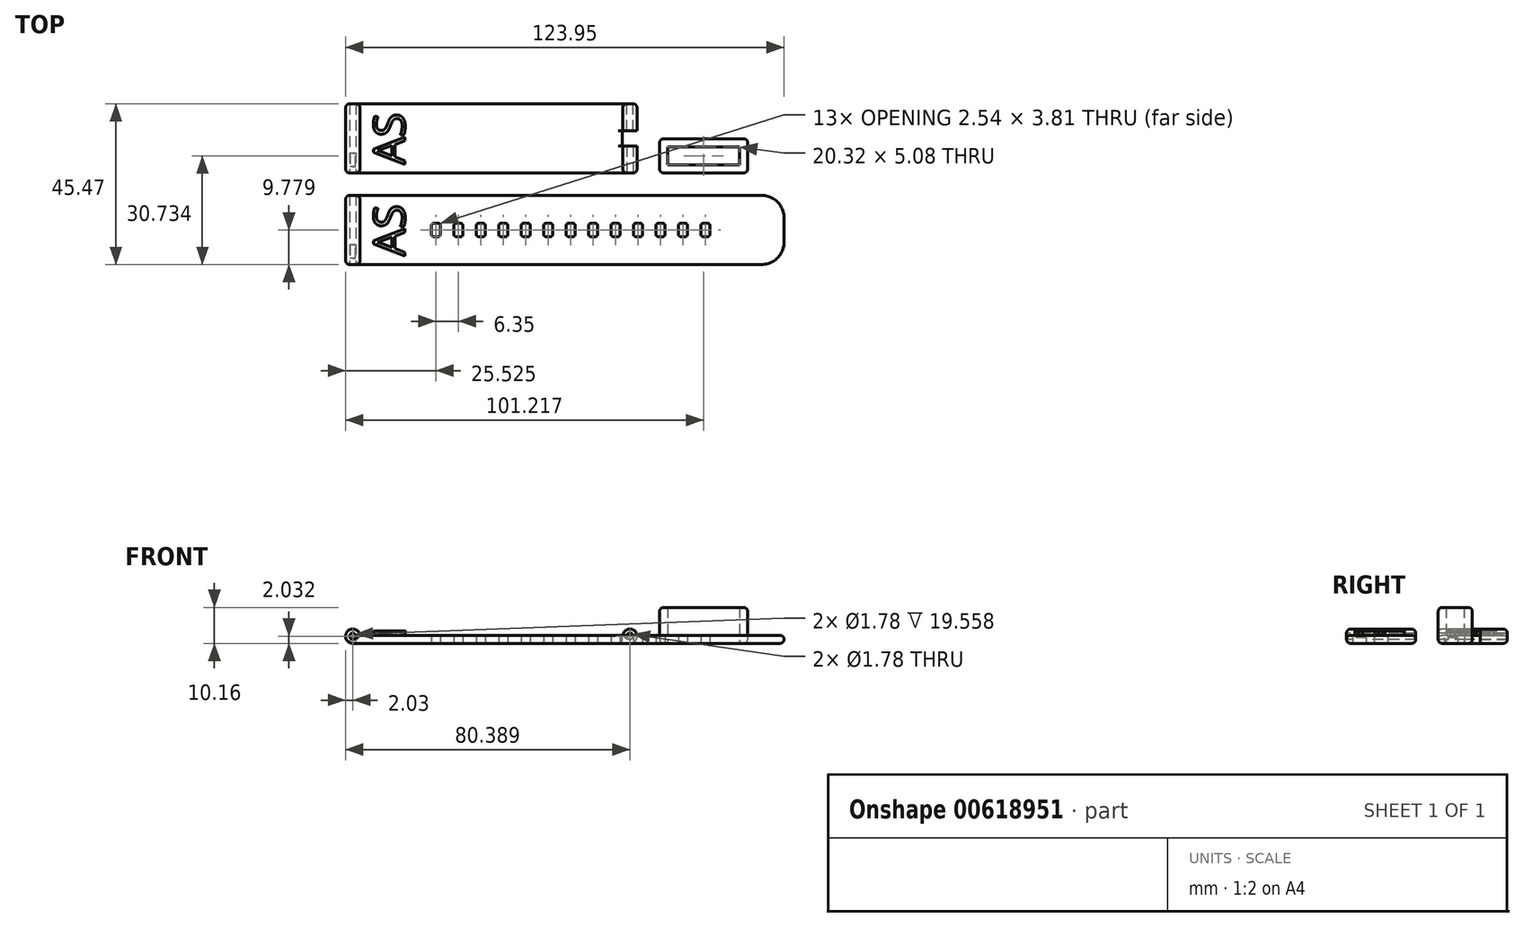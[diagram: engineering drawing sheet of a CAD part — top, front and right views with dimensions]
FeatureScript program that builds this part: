
annotation { "Feature Type Name" : "Feature", "Feature Type Description" : "" }
export const myFeature = defineFeature(function(context is Context, id is Id, definition is map)
    precondition{}
    {
        {
            var Q0;
            Q0=qCreatedBy(makeId("Top.planeOp"),FACE);
            var sketch = newSketch(context, id + "F0", { "sketchPlane" : qUnion([Q0])});
            skLineSegment(sketch, "E0.bottom", {"start": v(0, 0) * mm, "end": v(115.57, 0) * mm});
            skLineSegment(sketch, "E0.top", {"start": v(0, 19.56) * mm, "end": v(115.57, 19.56) * mm});
            skLineSegment(sketch, "E0.left", {"start": v(0, 0) * mm, "end": v(0, 19.56) * mm});
            skLineSegment(sketch, "E0.right", {"start": v(121.92, 6.35) * mm, "end": v(121.92, 13.2) * mm});
            skPoint(sketch, "E1.visualSharp", {"position": v(121.92, 19.56) * mm});
            skArc(sketch, "E1.filletArc", {"start": v(121.92, 13.2) * mm, "mid": v(120.06, 17.7) * mm, "end": v(115.57, 19.56) * mm});
            skPoint(sketch, "E2.visualSharp", {"position": v(121.92, 0) * mm});
            skArc(sketch, "E2.filletArc", {"start": v(115.57, 0) * mm, "mid": v(120.06, 1.86) * mm, "end": v(121.92, 6.35) * mm});
            skLineSegment(sketch, "E3.bottom", {"start": v(24.13, 7.87) * mm, "end": v(22.86, 7.87) * mm});
            skLineSegment(sketch, "E3.top", {"start": v(24.13, 11.68) * mm, "end": v(22.86, 11.68) * mm});
            skLineSegment(sketch, "E3.left", {"start": v(24.77, 8.5) * mm, "end": v(24.77, 11.05) * mm});
            skLineSegment(sketch, "E3.right", {"start": v(22.23, 8.5) * mm, "end": v(22.23, 11.05) * mm});
            skPoint(sketch, "E3.middle", {"position": v(23.5, 9.78) * mm});
            skPoint(sketch, "E3.middle.positionSnap0", {"position": v(0, 9.78) * mm});
            skPoint(sketch, "E3.centerSnap0", {"position": v(0, 9.78) * mm});
            skPoint(sketch, "E4.visualSharp", {"position": v(22.23, 11.68) * mm});
            skArc(sketch, "E4.filletArc", {"start": v(22.86, 11.68) * mm, "mid": v(22.41, 11.5) * mm, "end": v(22.22, 11.05) * mm});
            skPoint(sketch, "E5.visualSharp", {"position": v(24.77, 11.68) * mm});
            skArc(sketch, "E5.filletArc", {"start": v(24.77, 11.05) * mm, "mid": v(24.58, 11.5) * mm, "end": v(24.13, 11.68) * mm});
            skPoint(sketch, "E6.visualSharp", {"position": v(24.77, 7.87) * mm});
            skArc(sketch, "E6.filletArc", {"start": v(24.13, 7.87) * mm, "mid": v(24.58, 8.06) * mm, "end": v(24.77, 8.5) * mm});
            skPoint(sketch, "E7.visualSharp", {"position": v(22.23, 7.87) * mm});
            skArc(sketch, "E7.filletArc", {"start": v(22.23, 8.5) * mm, "mid": v(22.41, 8.06) * mm, "end": v(22.86, 7.87) * mm});
            skPoint(sketch, "E8.1.0.0", {"position": v(28.58, 7.87) * mm});
            skPoint(sketch, "E8.1.0.1", {"position": v(31.12, 7.87) * mm});
            skPoint(sketch, "E8.1.0.2", {"position": v(28.58, 11.68) * mm});
            skPoint(sketch, "E8.1.0.3", {"position": v(31.12, 11.68) * mm});
            skPoint(sketch, "E8.1.0.4", {"position": v(29.85, 9.78) * mm});
            skLineSegment(sketch, "E8.1.0.5", {"start": v(30.48, 11.68) * mm, "end": v(29.21, 11.68) * mm});
            skLineSegment(sketch, "E8.1.0.6", {"start": v(31.12, 8.5) * mm, "end": v(31.12, 11.05) * mm});
            skLineSegment(sketch, "E8.1.0.7", {"start": v(28.58, 8.5) * mm, "end": v(28.58, 11.05) * mm});
            skArc(sketch, "E8.1.0.8", {"start": v(31.12, 11.05) * mm, "mid": v(30.93, 11.5) * mm, "end": v(30.48, 11.68) * mm});
            skArc(sketch, "E8.1.0.9", {"start": v(29.21, 11.68) * mm, "mid": v(28.76, 11.5) * mm, "end": v(28.57, 11.05) * mm});
            skArc(sketch, "E8.1.0.10", {"start": v(30.48, 7.87) * mm, "mid": v(30.93, 8.06) * mm, "end": v(31.12, 8.5) * mm});
            skLineSegment(sketch, "E8.1.0.11", {"start": v(30.48, 7.87) * mm, "end": v(29.21, 7.87) * mm});
            skArc(sketch, "E8.1.0.12", {"start": v(28.58, 8.5) * mm, "mid": v(28.76, 8.06) * mm, "end": v(29.21, 7.87) * mm});
            skPoint(sketch, "E8.2.0.0", {"position": v(34.93, 7.87) * mm});
            skPoint(sketch, "E8.2.0.1", {"position": v(37.47, 7.87) * mm});
            skPoint(sketch, "E8.2.0.2", {"position": v(34.93, 11.68) * mm});
            skPoint(sketch, "E8.2.0.3", {"position": v(37.47, 11.68) * mm});
            skPoint(sketch, "E8.2.0.4", {"position": v(36.2, 9.78) * mm});
            skLineSegment(sketch, "E8.2.0.5", {"start": v(36.83, 11.68) * mm, "end": v(35.56, 11.68) * mm});
            skLineSegment(sketch, "E8.2.0.6", {"start": v(37.47, 8.5) * mm, "end": v(37.47, 11.05) * mm});
            skLineSegment(sketch, "E8.2.0.7", {"start": v(34.93, 8.5) * mm, "end": v(34.93, 11.05) * mm});
            skArc(sketch, "E8.2.0.8", {"start": v(37.46, 11.05) * mm, "mid": v(37.28, 11.5) * mm, "end": v(36.83, 11.68) * mm});
            skArc(sketch, "E8.2.0.9", {"start": v(35.56, 11.68) * mm, "mid": v(35.11, 11.5) * mm, "end": v(34.92, 11.05) * mm});
            skArc(sketch, "E8.2.0.10", {"start": v(36.83, 7.87) * mm, "mid": v(37.28, 8.06) * mm, "end": v(37.47, 8.5) * mm});
            skLineSegment(sketch, "E8.2.0.11", {"start": v(36.83, 7.87) * mm, "end": v(35.56, 7.87) * mm});
            skArc(sketch, "E8.2.0.12", {"start": v(34.93, 8.5) * mm, "mid": v(35.11, 8.06) * mm, "end": v(35.56, 7.87) * mm});
            skPoint(sketch, "E8.3.0.0", {"position": v(41.28, 7.87) * mm});
            skPoint(sketch, "E8.3.0.1", {"position": v(43.82, 7.87) * mm});
            skPoint(sketch, "E8.3.0.2", {"position": v(41.28, 11.68) * mm});
            skPoint(sketch, "E8.3.0.3", {"position": v(43.82, 11.68) * mm});
            skPoint(sketch, "E8.3.0.4", {"position": v(42.55, 9.78) * mm});
            skLineSegment(sketch, "E8.3.0.5", {"start": v(43.18, 11.68) * mm, "end": v(41.91, 11.68) * mm});
            skLineSegment(sketch, "E8.3.0.6", {"start": v(43.82, 8.5) * mm, "end": v(43.82, 11.05) * mm});
            skLineSegment(sketch, "E8.3.0.7", {"start": v(41.28, 8.5) * mm, "end": v(41.28, 11.05) * mm});
            skArc(sketch, "E8.3.0.8", {"start": v(43.82, 11.05) * mm, "mid": v(43.63, 11.5) * mm, "end": v(43.18, 11.68) * mm});
            skArc(sketch, "E8.3.0.9", {"start": v(41.91, 11.68) * mm, "mid": v(41.46, 11.5) * mm, "end": v(41.28, 11.05) * mm});
            skArc(sketch, "E8.3.0.10", {"start": v(43.18, 7.87) * mm, "mid": v(43.63, 8.06) * mm, "end": v(43.82, 8.5) * mm});
            skLineSegment(sketch, "E8.3.0.11", {"start": v(43.18, 7.87) * mm, "end": v(41.91, 7.87) * mm});
            skArc(sketch, "E8.3.0.12", {"start": v(41.28, 8.5) * mm, "mid": v(41.46, 8.06) * mm, "end": v(41.91, 7.87) * mm});
            skPoint(sketch, "E8.4.0.0", {"position": v(47.63, 7.87) * mm});
            skPoint(sketch, "E8.4.0.1", {"position": v(50.17, 7.87) * mm});
            skPoint(sketch, "E8.4.0.2", {"position": v(47.63, 11.68) * mm});
            skPoint(sketch, "E8.4.0.3", {"position": v(50.17, 11.68) * mm});
            skPoint(sketch, "E8.4.0.4", {"position": v(48.9, 9.78) * mm});
            skLineSegment(sketch, "E8.4.0.5", {"start": v(49.53, 11.68) * mm, "end": v(48.26, 11.68) * mm});
            skLineSegment(sketch, "E8.4.0.6", {"start": v(50.17, 8.5) * mm, "end": v(50.17, 11.05) * mm});
            skLineSegment(sketch, "E8.4.0.7", {"start": v(47.63, 8.5) * mm, "end": v(47.63, 11.05) * mm});
            skArc(sketch, "E8.4.0.8", {"start": v(50.16, 11.05) * mm, "mid": v(49.98, 11.5) * mm, "end": v(49.53, 11.68) * mm});
            skArc(sketch, "E8.4.0.9", {"start": v(48.26, 11.68) * mm, "mid": v(47.81, 11.5) * mm, "end": v(47.62, 11.05) * mm});
            skArc(sketch, "E8.4.0.10", {"start": v(49.53, 7.87) * mm, "mid": v(49.98, 8.06) * mm, "end": v(50.17, 8.5) * mm});
            skLineSegment(sketch, "E8.4.0.11", {"start": v(49.53, 7.87) * mm, "end": v(48.26, 7.87) * mm});
            skArc(sketch, "E8.4.0.12", {"start": v(47.63, 8.5) * mm, "mid": v(47.81, 8.06) * mm, "end": v(48.26, 7.87) * mm});
            skPoint(sketch, "E8.5.0.0", {"position": v(53.98, 7.87) * mm});
            skPoint(sketch, "E8.5.0.1", {"position": v(56.52, 7.87) * mm});
            skPoint(sketch, "E8.5.0.2", {"position": v(53.98, 11.68) * mm});
            skPoint(sketch, "E8.5.0.3", {"position": v(56.52, 11.68) * mm});
            skPoint(sketch, "E8.5.0.4", {"position": v(55.25, 9.78) * mm});
            skLineSegment(sketch, "E8.5.0.5", {"start": v(55.88, 11.68) * mm, "end": v(54.61, 11.68) * mm});
            skLineSegment(sketch, "E8.5.0.6", {"start": v(56.52, 8.5) * mm, "end": v(56.52, 11.05) * mm});
            skLineSegment(sketch, "E8.5.0.7", {"start": v(53.98, 8.5) * mm, "end": v(53.98, 11.05) * mm});
            skArc(sketch, "E8.5.0.8", {"start": v(56.52, 11.05) * mm, "mid": v(56.33, 11.5) * mm, "end": v(55.88, 11.68) * mm});
            skArc(sketch, "E8.5.0.9", {"start": v(54.61, 11.68) * mm, "mid": v(54.16, 11.5) * mm, "end": v(53.98, 11.05) * mm});
            skArc(sketch, "E8.5.0.10", {"start": v(55.88, 7.87) * mm, "mid": v(56.33, 8.06) * mm, "end": v(56.52, 8.5) * mm});
            skLineSegment(sketch, "E8.5.0.11", {"start": v(55.88, 7.87) * mm, "end": v(54.61, 7.87) * mm});
            skArc(sketch, "E8.5.0.12", {"start": v(53.98, 8.5) * mm, "mid": v(54.16, 8.06) * mm, "end": v(54.61, 7.87) * mm});
            skPoint(sketch, "E8.6.0.0", {"position": v(60.33, 7.87) * mm});
            skPoint(sketch, "E8.6.0.1", {"position": v(62.87, 7.87) * mm});
            skPoint(sketch, "E8.6.0.2", {"position": v(60.33, 11.68) * mm});
            skPoint(sketch, "E8.6.0.3", {"position": v(62.87, 11.68) * mm});
            skPoint(sketch, "E8.6.0.4", {"position": v(61.6, 9.78) * mm});
            skLineSegment(sketch, "E8.6.0.5", {"start": v(62.23, 11.68) * mm, "end": v(60.96, 11.68) * mm});
            skLineSegment(sketch, "E8.6.0.6", {"start": v(62.87, 8.5) * mm, "end": v(62.87, 11.05) * mm});
            skLineSegment(sketch, "E8.6.0.7", {"start": v(60.33, 8.5) * mm, "end": v(60.33, 11.05) * mm});
            skArc(sketch, "E8.6.0.8", {"start": v(62.87, 11.05) * mm, "mid": v(62.68, 11.5) * mm, "end": v(62.23, 11.68) * mm});
            skArc(sketch, "E8.6.0.9", {"start": v(60.96, 11.68) * mm, "mid": v(60.51, 11.5) * mm, "end": v(60.33, 11.05) * mm});
            skArc(sketch, "E8.6.0.10", {"start": v(62.23, 7.87) * mm, "mid": v(62.68, 8.06) * mm, "end": v(62.87, 8.5) * mm});
            skLineSegment(sketch, "E8.6.0.11", {"start": v(62.23, 7.87) * mm, "end": v(60.96, 7.87) * mm});
            skArc(sketch, "E8.6.0.12", {"start": v(60.33, 8.5) * mm, "mid": v(60.51, 8.06) * mm, "end": v(60.96, 7.87) * mm});
            skPoint(sketch, "E8.7.0.0", {"position": v(66.68, 7.87) * mm});
            skPoint(sketch, "E8.7.0.1", {"position": v(69.22, 7.87) * mm});
            skPoint(sketch, "E8.7.0.2", {"position": v(66.68, 11.68) * mm});
            skPoint(sketch, "E8.7.0.3", {"position": v(69.22, 11.68) * mm});
            skPoint(sketch, "E8.7.0.4", {"position": v(67.95, 9.78) * mm});
            skLineSegment(sketch, "E8.7.0.5", {"start": v(68.58, 11.68) * mm, "end": v(67.31, 11.68) * mm});
            skLineSegment(sketch, "E8.7.0.6", {"start": v(69.22, 8.5) * mm, "end": v(69.22, 11.05) * mm});
            skLineSegment(sketch, "E8.7.0.7", {"start": v(66.68, 8.5) * mm, "end": v(66.68, 11.05) * mm});
            skArc(sketch, "E8.7.0.8", {"start": v(69.22, 11.05) * mm, "mid": v(69.03, 11.5) * mm, "end": v(68.58, 11.68) * mm});
            skArc(sketch, "E8.7.0.9", {"start": v(67.31, 11.68) * mm, "mid": v(66.86, 11.5) * mm, "end": v(66.68, 11.05) * mm});
            skArc(sketch, "E8.7.0.10", {"start": v(68.58, 7.87) * mm, "mid": v(69.03, 8.06) * mm, "end": v(69.22, 8.5) * mm});
            skLineSegment(sketch, "E8.7.0.11", {"start": v(68.58, 7.87) * mm, "end": v(67.31, 7.87) * mm});
            skArc(sketch, "E8.7.0.12", {"start": v(66.68, 8.5) * mm, "mid": v(66.86, 8.06) * mm, "end": v(67.31, 7.87) * mm});
            skPoint(sketch, "E8.8.0.0", {"position": v(73.03, 7.87) * mm});
            skPoint(sketch, "E8.8.0.1", {"position": v(75.57, 7.87) * mm});
            skPoint(sketch, "E8.8.0.2", {"position": v(73.03, 11.68) * mm});
            skPoint(sketch, "E8.8.0.3", {"position": v(75.57, 11.68) * mm});
            skPoint(sketch, "E8.8.0.4", {"position": v(74.3, 9.78) * mm});
            skLineSegment(sketch, "E8.8.0.5", {"start": v(74.93, 11.68) * mm, "end": v(73.66, 11.68) * mm});
            skLineSegment(sketch, "E8.8.0.6", {"start": v(75.57, 8.5) * mm, "end": v(75.57, 11.05) * mm});
            skLineSegment(sketch, "E8.8.0.7", {"start": v(73.03, 8.5) * mm, "end": v(73.03, 11.05) * mm});
            skArc(sketch, "E8.8.0.8", {"start": v(75.57, 11.05) * mm, "mid": v(75.38, 11.5) * mm, "end": v(74.93, 11.68) * mm});
            skArc(sketch, "E8.8.0.9", {"start": v(73.66, 11.68) * mm, "mid": v(73.21, 11.5) * mm, "end": v(73.03, 11.05) * mm});
            skArc(sketch, "E8.8.0.10", {"start": v(74.93, 7.87) * mm, "mid": v(75.38, 8.06) * mm, "end": v(75.57, 8.5) * mm});
            skLineSegment(sketch, "E8.8.0.11", {"start": v(74.93, 7.87) * mm, "end": v(73.66, 7.87) * mm});
            skArc(sketch, "E8.8.0.12", {"start": v(73.03, 8.5) * mm, "mid": v(73.21, 8.06) * mm, "end": v(73.66, 7.87) * mm});
            skPoint(sketch, "E8.9.0.0", {"position": v(79.38, 7.87) * mm});
            skPoint(sketch, "E8.9.0.1", {"position": v(81.92, 7.87) * mm});
            skPoint(sketch, "E8.9.0.2", {"position": v(79.38, 11.68) * mm});
            skPoint(sketch, "E8.9.0.3", {"position": v(81.92, 11.68) * mm});
            skPoint(sketch, "E8.9.0.4", {"position": v(80.65, 9.78) * mm});
            skLineSegment(sketch, "E8.9.0.5", {"start": v(81.28, 11.68) * mm, "end": v(80.01, 11.68) * mm});
            skLineSegment(sketch, "E8.9.0.6", {"start": v(81.92, 8.5) * mm, "end": v(81.92, 11.05) * mm});
            skLineSegment(sketch, "E8.9.0.7", {"start": v(79.38, 8.5) * mm, "end": v(79.38, 11.05) * mm});
            skArc(sketch, "E8.9.0.8", {"start": v(81.92, 11.05) * mm, "mid": v(81.73, 11.5) * mm, "end": v(81.28, 11.68) * mm});
            skArc(sketch, "E8.9.0.9", {"start": v(80.01, 11.68) * mm, "mid": v(79.56, 11.5) * mm, "end": v(79.38, 11.05) * mm});
            skArc(sketch, "E8.9.0.10", {"start": v(81.28, 7.87) * mm, "mid": v(81.73, 8.06) * mm, "end": v(81.92, 8.5) * mm});
            skLineSegment(sketch, "E8.9.0.11", {"start": v(81.28, 7.87) * mm, "end": v(80.01, 7.87) * mm});
            skArc(sketch, "E8.9.0.12", {"start": v(79.38, 8.5) * mm, "mid": v(79.56, 8.06) * mm, "end": v(80.01, 7.87) * mm});
            skPoint(sketch, "E8.10.0.0", {"position": v(85.73, 7.87) * mm});
            skPoint(sketch, "E8.10.0.1", {"position": v(88.27, 7.87) * mm});
            skPoint(sketch, "E8.10.0.2", {"position": v(85.73, 11.68) * mm});
            skPoint(sketch, "E8.10.0.3", {"position": v(88.27, 11.68) * mm});
            skPoint(sketch, "E8.10.0.4", {"position": v(87, 9.78) * mm});
            skLineSegment(sketch, "E8.10.0.5", {"start": v(87.63, 11.68) * mm, "end": v(86.36, 11.68) * mm});
            skLineSegment(sketch, "E8.10.0.6", {"start": v(88.27, 8.5) * mm, "end": v(88.27, 11.05) * mm});
            skLineSegment(sketch, "E8.10.0.7", {"start": v(85.73, 8.5) * mm, "end": v(85.73, 11.05) * mm});
            skArc(sketch, "E8.10.0.8", {"start": v(88.27, 11.05) * mm, "mid": v(88.08, 11.5) * mm, "end": v(87.63, 11.68) * mm});
            skArc(sketch, "E8.10.0.9", {"start": v(86.36, 11.68) * mm, "mid": v(85.91, 11.5) * mm, "end": v(85.73, 11.05) * mm});
            skArc(sketch, "E8.10.0.10", {"start": v(87.63, 7.87) * mm, "mid": v(88.08, 8.06) * mm, "end": v(88.27, 8.5) * mm});
            skLineSegment(sketch, "E8.10.0.11", {"start": v(87.63, 7.87) * mm, "end": v(86.36, 7.87) * mm});
            skArc(sketch, "E8.10.0.12", {"start": v(85.73, 8.5) * mm, "mid": v(85.91, 8.06) * mm, "end": v(86.36, 7.87) * mm});
            skPoint(sketch, "E8.11.0.0", {"position": v(92.08, 7.87) * mm});
            skPoint(sketch, "E8.11.0.1", {"position": v(94.62, 7.87) * mm});
            skPoint(sketch, "E8.11.0.2", {"position": v(92.08, 11.68) * mm});
            skPoint(sketch, "E8.11.0.3", {"position": v(94.62, 11.68) * mm});
            skPoint(sketch, "E8.11.0.4", {"position": v(93.35, 9.78) * mm});
            skLineSegment(sketch, "E8.11.0.5", {"start": v(93.98, 11.68) * mm, "end": v(92.71, 11.68) * mm});
            skLineSegment(sketch, "E8.11.0.6", {"start": v(94.62, 8.5) * mm, "end": v(94.62, 11.05) * mm});
            skLineSegment(sketch, "E8.11.0.7", {"start": v(92.08, 8.5) * mm, "end": v(92.08, 11.05) * mm});
            skArc(sketch, "E8.11.0.8", {"start": v(94.62, 11.05) * mm, "mid": v(94.43, 11.5) * mm, "end": v(93.98, 11.68) * mm});
            skArc(sketch, "E8.11.0.9", {"start": v(92.71, 11.68) * mm, "mid": v(92.26, 11.5) * mm, "end": v(92.08, 11.05) * mm});
            skArc(sketch, "E8.11.0.10", {"start": v(93.98, 7.87) * mm, "mid": v(94.43, 8.06) * mm, "end": v(94.62, 8.5) * mm});
            skLineSegment(sketch, "E8.11.0.11", {"start": v(93.98, 7.87) * mm, "end": v(92.71, 7.87) * mm});
            skArc(sketch, "E8.11.0.12", {"start": v(92.08, 8.5) * mm, "mid": v(92.26, 8.06) * mm, "end": v(92.71, 7.87) * mm});
            skPoint(sketch, "E8.12.0.0", {"position": v(98.43, 7.87) * mm});
            skPoint(sketch, "E8.12.0.1", {"position": v(100.97, 7.87) * mm});
            skPoint(sketch, "E8.12.0.2", {"position": v(98.43, 11.68) * mm});
            skPoint(sketch, "E8.12.0.3", {"position": v(100.97, 11.68) * mm});
            skPoint(sketch, "E8.12.0.4", {"position": v(99.7, 9.78) * mm});
            skLineSegment(sketch, "E8.12.0.5", {"start": v(100.33, 11.68) * mm, "end": v(99.06, 11.68) * mm});
            skLineSegment(sketch, "E8.12.0.6", {"start": v(100.97, 8.5) * mm, "end": v(100.97, 11.05) * mm});
            skLineSegment(sketch, "E8.12.0.7", {"start": v(98.43, 8.5) * mm, "end": v(98.43, 11.05) * mm});
            skArc(sketch, "E8.12.0.8", {"start": v(100.97, 11.05) * mm, "mid": v(100.78, 11.5) * mm, "end": v(100.33, 11.68) * mm});
            skArc(sketch, "E8.12.0.9", {"start": v(99.06, 11.68) * mm, "mid": v(98.61, 11.5) * mm, "end": v(98.43, 11.05) * mm});
            skArc(sketch, "E8.12.0.10", {"start": v(100.33, 7.87) * mm, "mid": v(100.78, 8.06) * mm, "end": v(100.97, 8.5) * mm});
            skLineSegment(sketch, "E8.12.0.11", {"start": v(100.33, 7.87) * mm, "end": v(99.06, 7.87) * mm});
            skArc(sketch, "E8.12.0.12", {"start": v(98.43, 8.5) * mm, "mid": v(98.61, 8.06) * mm, "end": v(99.06, 7.87) * mm});
            skLineSegment(sketch, "E8.direction1", {"start": v(22.23, 7.87) * mm, "end": v(28.58, 7.87) * mm, "construction": true});
            skSolve(sketch);
        }
        {
            var Q0;
            Q0=makeQuery(id+"F0.imprint","IMPRINT",FACE,{"disambiguationData":[TD([[makeQuery(id+"F0.imprint","IMPRINT",EDGE,{"derivedFrom":sQuery(id+"F0.wireOp",EDGE,"E0.bottom")}),1.0]])]});
            extrude(context, id + "F1", {"entities" : qUnion([Q0]), "depth" : 2.3 * mm, "offsetDistance" : 25.4 * mm});
        }
        {
            var Q0;
            Q0=makeQuery(id+"F1.opExtrude","SWEPT_FACE",FACE,{"disambiguationData":[OSD([sQuery(id+"F0.wireOp",EDGE,"E0.bottom")])]});
            var sketch = newSketch(context, id + "F2", { "sketchPlane" : qUnion([Q0])});
            skCircle(sketch, "E9", {"center": v(0, 2.03) * mm, "radius": 0.89 * mm});
            skCircle(sketch, "E10.0", {"center": v(0, 2.03) * mm, "radius": 2.03 * mm});
            skSolve(sketch);
        }
        {
            var Q0;
            {var subQ0=sQuery(id+"F2.wireOp",EDGE,"E9");var subQ1=makeQuery(id+"F1.opExtrude","SWEPT_EDGE",EDGE,{"disambiguationData":[OSD([sQuery(id+"F0.wireOp",EDGE,"E0.bottom"),sQuery(id+"F0.wireOp",EDGE,"E0.left")])]});var subQ2=makeQuery(id+"F2.imprint","INTERSECT",VERTEX,{"disambiguationData":[OD(0.0)],"derivedFrom":[subQ1,subQ0]});Q0=makeQuery(id+"F2.imprint","IMPRINT",FACE,{"disambiguationData":[TD([[makeQuery(id+"F2.imprint","IMPRINT",EDGE,{"disambiguationData":[TD([[subQ2,-1.0]])],"derivedFrom":subQ0}),1.0]])]});}
            extrude(context, id + "F3", {"entities" : qUnion([Q0]), "operationType" : NewBodyOperationType.REMOVE, "endBound" : BoundingType.THROUGH_ALL, "oppositeDirection" : true, "depth" : 25.4 * mm, "offsetDistance" : 25.4 * mm});
        }
        {
            var Q0;
            {var subQ0=sQuery(id+"F0.wireOp",EDGE,"E0.bottom");var subQ6=sQuery(id+"F2.wireOp",EDGE,"E10.0");var subQ7=makeQuery(id+"F1.opExtrude","CAP_EDGE",EDGE,{"disambiguationData":[OSD([subQ0])],"isStart":true});var subQ8=makeQuery(id+"F2.imprint","INTERSECT",VERTEX,{"derivedFrom":[subQ7,subQ6]});Q0=makeQuery(id+"F2.imprint","IMPRINT",FACE,{"disambiguationData":[TD([[makeQuery(id+"F2.imprint","IMPRINT",EDGE,{"disambiguationData":[TD([[subQ8,1.0]])],"derivedFrom":subQ6}),1.0]])]});}
            var Q1;
            Q1=makeQuery(id+"F1.opExtrude","SWEPT_FACE",FACE,{"disambiguationData":[OSD([sQuery(id+"F0.wireOp",EDGE,"E0.top")])]});
            extrude(context, id + "F4", {"entities" : qUnion([Q0]), "operationType" : NewBodyOperationType.ADD, "endBound" : BoundingType.UP_TO_SURFACE, "oppositeDirection" : true, "depth" : 25.4 * mm, "endBoundEntityFace" : qUnion([Q1]), "offsetDistance" : 25.4 * mm});
        }
        {
            var Q0;
            Q0=makeQuery(id+"F1.opExtrude","CAP_FACE",FACE,{"disambiguationData":[OSD([sQuery(id+"F0.wireOp",EDGE,"E0.bottom"),sQuery(id+"F0.wireOp",EDGE,"E0.top"),sQuery(id+"F0.wireOp",EDGE,"E0.left"),sQuery(id+"F0.wireOp",EDGE,"E0.right"),sQuery(id+"F0.wireOp",EDGE,"E1.filletArc"),sQuery(id+"F0.wireOp",EDGE,"E2.filletArc"),sQuery(id+"F0.wireOp",EDGE,"E3.bottom"),sQuery(id+"F0.wireOp",EDGE,"E3.top"),sQuery(id+"F0.wireOp",EDGE,"E3.left"),sQuery(id+"F0.wireOp",EDGE,"E3.right"),sQuery(id+"F0.wireOp",EDGE,"E4.filletArc"),sQuery(id+"F0.wireOp",EDGE,"E5.filletArc"),sQuery(id+"F0.wireOp",EDGE,"E6.filletArc"),sQuery(id+"F0.wireOp",EDGE,"E7.filletArc"),sQuery(id+"F0.wireOp",EDGE,"E8.1.0.5"),sQuery(id+"F0.wireOp",EDGE,"E8.1.0.6"),sQuery(id+"F0.wireOp",EDGE,"E8.1.0.7"),sQuery(id+"F0.wireOp",EDGE,"E8.1.0.8"),sQuery(id+"F0.wireOp",EDGE,"E8.1.0.9"),sQuery(id+"F0.wireOp",EDGE,"E8.1.0.10"),sQuery(id+"F0.wireOp",EDGE,"E8.1.0.11"),sQuery(id+"F0.wireOp",EDGE,"E8.1.0.12"),sQuery(id+"F0.wireOp",EDGE,"E8.2.0.5"),sQuery(id+"F0.wireOp",EDGE,"E8.2.0.6"),sQuery(id+"F0.wireOp",EDGE,"E8.2.0.7"),sQuery(id+"F0.wireOp",EDGE,"E8.2.0.8"),sQuery(id+"F0.wireOp",EDGE,"E8.2.0.9"),sQuery(id+"F0.wireOp",EDGE,"E8.2.0.10"),sQuery(id+"F0.wireOp",EDGE,"E8.2.0.11"),sQuery(id+"F0.wireOp",EDGE,"E8.2.0.12"),sQuery(id+"F0.wireOp",EDGE,"E8.3.0.5"),sQuery(id+"F0.wireOp",EDGE,"E8.3.0.6"),sQuery(id+"F0.wireOp",EDGE,"E8.3.0.7"),sQuery(id+"F0.wireOp",EDGE,"E8.3.0.8"),sQuery(id+"F0.wireOp",EDGE,"E8.3.0.9"),sQuery(id+"F0.wireOp",EDGE,"E8.3.0.10"),sQuery(id+"F0.wireOp",EDGE,"E8.3.0.11"),sQuery(id+"F0.wireOp",EDGE,"E8.3.0.12"),sQuery(id+"F0.wireOp",EDGE,"E8.4.0.5"),sQuery(id+"F0.wireOp",EDGE,"E8.4.0.6"),sQuery(id+"F0.wireOp",EDGE,"E8.4.0.7"),sQuery(id+"F0.wireOp",EDGE,"E8.4.0.8"),sQuery(id+"F0.wireOp",EDGE,"E8.4.0.9"),sQuery(id+"F0.wireOp",EDGE,"E8.4.0.10"),sQuery(id+"F0.wireOp",EDGE,"E8.4.0.11"),sQuery(id+"F0.wireOp",EDGE,"E8.4.0.12"),sQuery(id+"F0.wireOp",EDGE,"E8.5.0.5"),sQuery(id+"F0.wireOp",EDGE,"E8.5.0.6"),sQuery(id+"F0.wireOp",EDGE,"E8.5.0.7"),sQuery(id+"F0.wireOp",EDGE,"E8.5.0.8"),sQuery(id+"F0.wireOp",EDGE,"E8.5.0.9"),sQuery(id+"F0.wireOp",EDGE,"E8.5.0.10"),sQuery(id+"F0.wireOp",EDGE,"E8.5.0.11"),sQuery(id+"F0.wireOp",EDGE,"E8.5.0.12"),sQuery(id+"F0.wireOp",EDGE,"E8.6.0.5"),sQuery(id+"F0.wireOp",EDGE,"E8.6.0.6"),sQuery(id+"F0.wireOp",EDGE,"E8.6.0.7"),sQuery(id+"F0.wireOp",EDGE,"E8.6.0.8"),sQuery(id+"F0.wireOp",EDGE,"E8.6.0.9"),sQuery(id+"F0.wireOp",EDGE,"E8.6.0.10"),sQuery(id+"F0.wireOp",EDGE,"E8.6.0.11"),sQuery(id+"F0.wireOp",EDGE,"E8.6.0.12"),sQuery(id+"F0.wireOp",EDGE,"E8.7.0.5"),sQuery(id+"F0.wireOp",EDGE,"E8.7.0.6"),sQuery(id+"F0.wireOp",EDGE,"E8.7.0.7"),sQuery(id+"F0.wireOp",EDGE,"E8.7.0.8"),sQuery(id+"F0.wireOp",EDGE,"E8.7.0.9"),sQuery(id+"F0.wireOp",EDGE,"E8.7.0.10"),sQuery(id+"F0.wireOp",EDGE,"E8.7.0.11"),sQuery(id+"F0.wireOp",EDGE,"E8.7.0.12"),sQuery(id+"F0.wireOp",EDGE,"E8.8.0.5"),sQuery(id+"F0.wireOp",EDGE,"E8.8.0.6"),sQuery(id+"F0.wireOp",EDGE,"E8.8.0.7"),sQuery(id+"F0.wireOp",EDGE,"E8.8.0.8"),sQuery(id+"F0.wireOp",EDGE,"E8.8.0.9"),sQuery(id+"F0.wireOp",EDGE,"E8.8.0.10"),sQuery(id+"F0.wireOp",EDGE,"E8.8.0.11"),sQuery(id+"F0.wireOp",EDGE,"E8.8.0.12"),sQuery(id+"F0.wireOp",EDGE,"E8.9.0.5"),sQuery(id+"F0.wireOp",EDGE,"E8.9.0.6"),sQuery(id+"F0.wireOp",EDGE,"E8.9.0.7"),sQuery(id+"F0.wireOp",EDGE,"E8.9.0.8"),sQuery(id+"F0.wireOp",EDGE,"E8.9.0.9"),sQuery(id+"F0.wireOp",EDGE,"E8.9.0.10"),sQuery(id+"F0.wireOp",EDGE,"E8.9.0.11"),sQuery(id+"F0.wireOp",EDGE,"E8.9.0.12"),sQuery(id+"F0.wireOp",EDGE,"E8.10.0.5"),sQuery(id+"F0.wireOp",EDGE,"E8.10.0.6"),sQuery(id+"F0.wireOp",EDGE,"E8.10.0.7"),sQuery(id+"F0.wireOp",EDGE,"E8.10.0.8"),sQuery(id+"F0.wireOp",EDGE,"E8.10.0.9"),sQuery(id+"F0.wireOp",EDGE,"E8.10.0.10"),sQuery(id+"F0.wireOp",EDGE,"E8.10.0.11"),sQuery(id+"F0.wireOp",EDGE,"E8.10.0.12"),sQuery(id+"F0.wireOp",EDGE,"E8.11.0.5"),sQuery(id+"F0.wireOp",EDGE,"E8.11.0.6"),sQuery(id+"F0.wireOp",EDGE,"E8.11.0.7"),sQuery(id+"F0.wireOp",EDGE,"E8.11.0.8"),sQuery(id+"F0.wireOp",EDGE,"E8.11.0.9"),sQuery(id+"F0.wireOp",EDGE,"E8.11.0.10"),sQuery(id+"F0.wireOp",EDGE,"E8.11.0.11"),sQuery(id+"F0.wireOp",EDGE,"E8.11.0.12"),sQuery(id+"F0.wireOp",EDGE,"E8.12.0.5"),sQuery(id+"F0.wireOp",EDGE,"E8.12.0.6"),sQuery(id+"F0.wireOp",EDGE,"E8.12.0.7"),sQuery(id+"F0.wireOp",EDGE,"E8.12.0.8"),sQuery(id+"F0.wireOp",EDGE,"E8.12.0.9"),sQuery(id+"F0.wireOp",EDGE,"E8.12.0.10"),sQuery(id+"F0.wireOp",EDGE,"E8.12.0.11"),sQuery(id+"F0.wireOp",EDGE,"E8.12.0.12")])],"isStart":true});
            var sketch = newSketch(context, id + "F5", { "sketchPlane" : qUnion([Q0])});
            skLineSegment(sketch, "E11.bottom", {"start": v(-0.76, -1.78) * mm, "end": v(0.76, -1.78) * mm});
            skLineSegment(sketch, "E11.top", {"start": v(-0.76, -5.59) * mm, "end": v(0.76, -5.59) * mm});
            skLineSegment(sketch, "E11.left", {"start": v(-0.76, -1.78) * mm, "end": v(-0.76, -5.59) * mm});
            skLineSegment(sketch, "E11.right", {"start": v(0.76, -1.78) * mm, "end": v(0.76, -5.59) * mm});
            skPoint(sketch, "E11.middle", {"position": v(0, -3.68) * mm});
            skSolve(sketch);
        }
        {
            var Q0;
            {var subQ0=sQuery(id+"F5.wireOp",EDGE,"E11.left");Q0=makeQuery(id+"F5.imprint","IMPRINT",FACE,{"disambiguationData":[TD([[makeQuery(id+"F5.imprint","IMPRINT",EDGE,{"derivedFrom":subQ0}),1.0]])]});}
            var Q1;
            {var subQ0=sQuery(id+"F5.wireOp",EDGE,"E11.right");Q1=makeQuery(id+"F5.imprint","IMPRINT",FACE,{"disambiguationData":[TD([[makeQuery(id+"F5.imprint","IMPRINT",EDGE,{"derivedFrom":subQ0}),-1.0]])]});}
            extrude(context, id + "F6", {"entities" : qUnion([Q0, Q1]), "operationType" : NewBodyOperationType.REMOVE, "endBound" : BoundingType.UP_TO_NEXT, "oppositeDirection" : true, "depth" : 25.4 * mm, "offsetDistance" : 25.4 * mm});
        }
        {
            var Q0;
            Q0=qCreatedBy(makeId("Top.planeOp"),FACE);
            var sketch = newSketch(context, id + "F7", { "sketchPlane" : qUnion([Q0])});
            skLineSegment(sketch, "E12.bottom", {"start": v(0, 25.9) * mm, "end": v(76.2, 25.9) * mm});
            skLineSegment(sketch, "E12.top", {"start": v(0, 45.47) * mm, "end": v(76.2, 45.47) * mm});
            skLineSegment(sketch, "E12.left", {"start": v(0, 25.9) * mm, "end": v(0, 45.47) * mm});
            skLineSegment(sketch, "E12.right", {"start": v(76.2, 25.9) * mm, "end": v(76.2, 45.47) * mm});
            skSolve(sketch);
        }
        {
            var Q0;
            Q0=makeQuery(id+"F7.imprint","IMPRINT",FACE,{"disambiguationData":[TD([[makeQuery(id+"F7.imprint","IMPRINT",EDGE,{"derivedFrom":sQuery(id+"F7.wireOp",EDGE,"E12.bottom")}),1.0]])]});
            extrude(context, id + "F8", {"entities" : qUnion([Q0]), "depth" : 2.3 * mm, "offsetDistance" : 25.4 * mm});
        }
        {
            var Q0;
            Q0=makeQuery(id+"F8.opExtrude","SWEPT_FACE",FACE,{"disambiguationData":[OSD([sQuery(id+"F7.wireOp",EDGE,"E12.bottom")])]});
            var sketch = newSketch(context, id + "F9", { "sketchPlane" : qUnion([Q0])});
            skCircle(sketch, "E13", {"center": v(0, 2.03) * mm, "radius": 2.03 * mm});
            skCircle(sketch, "E14", {"center": v(0, 2.03) * mm, "radius": 0.89 * mm});
            skSolve(sketch);
        }
        {
            var Q0;
            {var subQ0=sQuery(id+"F9.wireOp",EDGE,"E14");var subQ1=sQuery(id+"F7.wireOp",EDGE,"E12.bottom");var subQ4=makeQuery(id+"F8.opExtrude","CAP_EDGE",EDGE,{"disambiguationData":[OSD([subQ1])],"isStart":false});var subQ5=makeQuery(id+"F9.imprint","INTERSECT",VERTEX,{"derivedFrom":[subQ4,subQ0]});Q0=makeQuery(id+"F9.imprint","IMPRINT",FACE,{"disambiguationData":[TD([[makeQuery(id+"F9.imprint","IMPRINT",EDGE,{"disambiguationData":[TD([[subQ5,1.0]])],"derivedFrom":subQ0}),1.0]])]});}
            extrude(context, id + "F10", {"entities" : qUnion([Q0]), "operationType" : NewBodyOperationType.REMOVE, "endBound" : BoundingType.THROUGH_ALL, "oppositeDirection" : true, "depth" : 25.4 * mm, "offsetDistance" : 25.4 * mm});
        }
        {
            var Q0;
            Q0=qSketchRegion(id+"F9",true);
            var Q1;
            Q1=makeQuery(id+"F8.opExtrude","SWEPT_FACE",FACE,{"disambiguationData":[OSD([sQuery(id+"F7.wireOp",EDGE,"E12.top")])]});
            extrude(context, id + "F11", {"entities" : qUnion([Q0]), "operationType" : NewBodyOperationType.ADD, "endBound" : BoundingType.UP_TO_SURFACE, "oppositeDirection" : true, "depth" : 25.4 * mm, "endBoundEntityFace" : qUnion([Q1]), "offsetDistance" : 25.4 * mm});
        }
        {
            var Q0;
            Q0=makeQuery(id+"F11.boolean.opBoolean","MERGE",FACE,{"derivedFrom":[makeQuery(id+"F8.opExtrude","SWEPT_FACE",FACE,{"disambiguationData":[OSD([sQuery(id+"F7.wireOp",EDGE,"E12.bottom")])]}),makeQuery(id+"F11.opExtrude","CAP_FACE",FACE,{"disambiguationData":[OSD([sQuery(id+"F9.wireOp",EDGE,"E13"),sQuery(id+"F9.wireOp",EDGE,"E14")])],"isStart":true})]});
            var sketch = newSketch(context, id + "F12", { "sketchPlane" : qUnion([Q0])});
            skCircle(sketch, "E15", {"center": v(78.36, 2.03) * mm, "radius": 2.03 * mm});
            skCircle(sketch, "E16", {"center": v(78.36, 2.03) * mm, "radius": 0.89 * mm});
            skLineSegment(sketch, "E17", {"start": v(78.36, 0) * mm, "end": v(76.2, 0) * mm});
            skLineSegment(sketch, "E18", {"start": v(76.2, 2.29) * mm, "end": v(76.34, 2.29) * mm});
            skSolve(sketch);
        }
        {
            var Q0;
            Q0=makeQuery(id+"F12.imprint","IMPRINT",FACE,{"disambiguationData":[TD([[makeQuery(id+"F12.imprint","IMPRINT",EDGE,{"derivedFrom":sQuery(id+"F12.wireOp",EDGE,"E16")}),-1.0]])]});
            var Q1;
            {var subQ0=sQuery(id+"F12.wireOp",EDGE,"E17");Q1=makeQuery(id+"F12.imprint","IMPRINT",FACE,{"disambiguationData":[TD([[makeQuery(id+"F12.imprint","IMPRINT",EDGE,{"derivedFrom":subQ0}),-1.0]])]});}
            extrude(context, id + "F13", {"entities" : qUnion([Q0, Q1]), "operationType" : NewBodyOperationType.ADD, "oppositeDirection" : true, "depth" : 7.62 * mm, "offsetDistance" : 25.4 * mm});
        }
        {
            var Q0;
            {var subQ0=sQuery(id+"F7.wireOp",EDGE,"E12.top");Q0=makeQuery(id+"F11.boolean.opBoolean","MERGE",FACE,{"derivedFrom":[makeQuery(id+"F8.opExtrude","SWEPT_FACE",FACE,{"disambiguationData":[OSD([subQ0])]}),makeQuery(id+"F11.opExtrude","CAP_FACE",FACE,{"disambiguationData":[OSD([subQ0])],"isStart":false})]});}
            var sketch = newSketch(context, id + "F14", { "sketchPlane" : qUnion([Q0])});
            skCircle(sketch, "E19.0", {"center": v(-78.36, 2.03) * mm, "radius": 0.89 * mm});
            skArc(sketch, "E20.0", {"start": v(-78.36, 0) * mm, "mid": v(-79.88, 3.38) * mm, "end": v(-76.34, 2.29) * mm});
            skCircle(sketch, "E21", {"center": v(-78.36, 2.03) * mm, "radius": 2.03 * mm});
            skLineSegment(sketch, "E22", {"start": v(-76.34, 2.29) * mm, "end": v(-76.2, 2.29) * mm});
            skLineSegment(sketch, "E23", {"start": v(-76.2, 2.29) * mm, "end": v(-76.2, 0) * mm});
            skLineSegment(sketch, "E24", {"start": v(-76.2, 0) * mm, "end": v(-78.36, 0) * mm});
            skSolve(sketch);
        }
        {
            var Q0;
            Q0=qSketchRegion(id+"F14",true);
            extrude(context, id + "F15", {"entities" : qUnion([Q0]), "operationType" : NewBodyOperationType.ADD, "oppositeDirection" : true, "depth" : 7.62 * mm, "offsetDistance" : 25.4 * mm});
        }
        {
            var Q0;
            Q0=qCreatedBy(makeId("Top.planeOp"),FACE);
            var sketch = newSketch(context, id + "F16", { "sketchPlane" : qUnion([Q0])});
            skLineSegment(sketch, "E25.bottom", {"start": v(89.03, 33.27) * mm, "end": v(109.35, 33.27) * mm});
            skLineSegment(sketch, "E25.top", {"start": v(89.03, 28.2) * mm, "end": v(109.35, 28.2) * mm});
            skLineSegment(sketch, "E25.left", {"start": v(89.03, 33.27) * mm, "end": v(89.03, 28.2) * mm});
            skLineSegment(sketch, "E25.right", {"start": v(109.35, 33.27) * mm, "end": v(109.35, 28.2) * mm});
            skPoint(sketch, "E25.middle", {"position": v(99.19, 30.73) * mm});
            skLineSegment(sketch, "E26.0", {"start": v(86.74, 35.56) * mm, "end": v(111.63, 35.56) * mm});
            skLineSegment(sketch, "E26.1", {"start": v(86.74, 35.56) * mm, "end": v(86.74, 25.9) * mm});
            skLineSegment(sketch, "E26.2", {"start": v(86.74, 25.9) * mm, "end": v(111.63, 25.9) * mm});
            skLineSegment(sketch, "E26.3", {"start": v(111.63, 35.56) * mm, "end": v(111.63, 25.9) * mm});
            skLineSegment(sketch, "E27.0", {"start": v(80.4, 25.9) * mm, "end": v(76.34, 25.9) * mm});
            skSolve(sketch);
        }
        {
            var Q0;
            Q0=qSketchRegion(id+"F16",true);
            extrude(context, id + "F17", {"entities" : qUnion([Q0]), "depth" : 10.16 * mm, "offsetDistance" : 25.4 * mm});
        }
        {
            var Q0;
            Q0=makeQuery(id+"F15.boolean.opBoolean","MERGE",FACE,{"derivedFrom":[makeQuery(id+"F13.boolean.opBoolean","MERGE",FACE,{"derivedFrom":[makeQuery(id+"F8.opExtrude","CAP_FACE",FACE,{"disambiguationData":[OSD([sQuery(id+"F7.wireOp",EDGE,"E12.bottom"),sQuery(id+"F7.wireOp",EDGE,"E12.top"),sQuery(id+"F7.wireOp",EDGE,"E12.left"),sQuery(id+"F7.wireOp",EDGE,"E12.right")])],"isStart":true}),makeQuery(id+"F13.opExtrude","SWEPT_FACE",FACE,{"disambiguationData":[OSD([sQuery(id+"F12.wireOp",EDGE,"E17")])]})]}),makeQuery(id+"F15.opExtrude","SWEPT_FACE",FACE,{"disambiguationData":[OSD([sQuery(id+"F14.wireOp",EDGE,"E24")])]})]});
            var sketch = newSketch(context, id + "F18", { "sketchPlane" : qUnion([Q0])});
            skLineSegment(sketch, "E28.bottom", {"start": v(-0.76, -27.69) * mm, "end": v(0.76, -27.69) * mm});
            skLineSegment(sketch, "E28.top", {"start": v(-0.76, -31.5) * mm, "end": v(0.76, -31.5) * mm});
            skLineSegment(sketch, "E28.left", {"start": v(-0.76, -27.69) * mm, "end": v(-0.76, -31.5) * mm});
            skLineSegment(sketch, "E28.right", {"start": v(0.76, -27.69) * mm, "end": v(0.76, -31.5) * mm});
            skPoint(sketch, "E28.middle", {"position": v(0, -29.6) * mm});
            skSolve(sketch);
        }
        {
            var Q0;
            Q0=qSketchRegion(id+"F18",true);
            extrude(context, id + "F19", {"entities" : qUnion([Q0]), "operationType" : NewBodyOperationType.REMOVE, "endBound" : BoundingType.UP_TO_NEXT, "oppositeDirection" : true, "depth" : 25.4 * mm, "offsetDistance" : 25.4 * mm});
        }
        {
            var Q0;
            Q0=makeQuery(id+"F13.boolean.opBoolean","MERGE",EDGE,{"derivedFrom":[makeQuery(id+"F8.opExtrude","CAP_EDGE",EDGE,{"disambiguationData":[OSD([sQuery(id+"F7.wireOp",EDGE,"E12.bottom")])],"isStart":false}),makeQuery(id+"F13.opExtrude","CAP_EDGE",EDGE,{"disambiguationData":[OSD([sQuery(id+"F12.wireOp",EDGE,"E18")])],"isStart":true})]});
            var Q1;
            Q1=makeQuery(id+"F13.boolean.opBoolean","MERGE",EDGE,{"derivedFrom":[makeQuery(id+"F8.opExtrude","CAP_EDGE",EDGE,{"disambiguationData":[OSD([sQuery(id+"F7.wireOp",EDGE,"E12.bottom")])],"isStart":true}),makeQuery(id+"F13.opExtrude","CAP_EDGE",EDGE,{"disambiguationData":[OSD([sQuery(id+"F12.wireOp",EDGE,"E17")])],"isStart":true})]});
            var Q2;
            Q2=makeQuery(id+"F15.boolean.opBoolean","MERGE",EDGE,{"derivedFrom":[makeQuery(id+"F8.opExtrude","CAP_EDGE",EDGE,{"disambiguationData":[OSD([sQuery(id+"F7.wireOp",EDGE,"E12.top")])],"isStart":false}),makeQuery(id+"F15.opExtrude","CAP_EDGE",EDGE,{"disambiguationData":[OSD([sQuery(id+"F14.wireOp",EDGE,"E22")])],"isStart":true})]});
            var Q3;
            Q3=makeQuery(id+"F15.boolean.opBoolean","MERGE",EDGE,{"derivedFrom":[makeQuery(id+"F8.opExtrude","CAP_EDGE",EDGE,{"disambiguationData":[OSD([sQuery(id+"F7.wireOp",EDGE,"E12.top")])],"isStart":true}),makeQuery(id+"F15.opExtrude","CAP_EDGE",EDGE,{"disambiguationData":[OSD([sQuery(id+"F14.wireOp",EDGE,"E24")])],"isStart":true})]});
            var Q4;
            Q4=makeQuery(id+"F1.opExtrude","CAP_EDGE",EDGE,{"disambiguationData":[OSD([sQuery(id+"F0.wireOp",EDGE,"E0.bottom")])],"isStart":true});
            var Q5;
            Q5=makeQuery(id+"F1.opExtrude","CAP_EDGE",EDGE,{"disambiguationData":[OSD([sQuery(id+"F0.wireOp",EDGE,"E0.bottom")])],"isStart":false});
            var Q6;
            Q6=makeQuery(id+"F17.opExtrude","CAP_EDGE",EDGE,{"disambiguationData":[OSD([sQuery(id+"F16.wireOp",EDGE,"E26.2")])],"isStart":true});
            var Q7;
            Q7=makeQuery(id+"F17.opExtrude","CAP_EDGE",EDGE,{"disambiguationData":[OSD([sQuery(id+"F16.wireOp",EDGE,"E26.3")])],"isStart":true});
            var Q8;
            Q8=makeQuery(id+"F17.opExtrude","CAP_EDGE",EDGE,{"disambiguationData":[OSD([sQuery(id+"F16.wireOp",EDGE,"E26.0")])],"isStart":true});
            var Q9;
            Q9=makeQuery(id+"F17.opExtrude","CAP_EDGE",EDGE,{"disambiguationData":[OSD([sQuery(id+"F16.wireOp",EDGE,"E26.1")])],"isStart":true});
            var Q10;
            Q10=makeQuery(id+"F17.opExtrude","CAP_EDGE",EDGE,{"disambiguationData":[OSD([sQuery(id+"F16.wireOp",EDGE,"E26.1")])],"isStart":false});
            var Q11;
            Q11=makeQuery(id+"F17.opExtrude","CAP_EDGE",EDGE,{"disambiguationData":[OSD([sQuery(id+"F16.wireOp",EDGE,"E26.0")])],"isStart":false});
            var Q12;
            Q12=makeQuery(id+"F17.opExtrude","CAP_EDGE",EDGE,{"disambiguationData":[OSD([sQuery(id+"F16.wireOp",EDGE,"E26.2")])],"isStart":false});
            var Q13;
            Q13=makeQuery(id+"F17.opExtrude","CAP_EDGE",EDGE,{"disambiguationData":[OSD([sQuery(id+"F16.wireOp",EDGE,"E26.3")])],"isStart":false});
            var Q14;
            Q14=makeQuery(id+"F8.opExtrude","CAP_EDGE",EDGE,{"disambiguationData":[OSD([sQuery(id+"F7.wireOp",EDGE,"E12.right")])],"isStart":true});
            var Q15;
            Q15=makeQuery(id+"F8.opExtrude","CAP_EDGE",EDGE,{"disambiguationData":[OSD([sQuery(id+"F7.wireOp",EDGE,"E12.right")])],"isStart":false});
            var Q16;
            Q16=makeQuery(id+"F17.opExtrude","SWEPT_EDGE",EDGE,{"disambiguationData":[OSD([sQuery(id+"F16.wireOp",EDGE,"E26.0"),sQuery(id+"F16.wireOp",EDGE,"E26.3")])]});
            var Q17;
            Q17=makeQuery(id+"F17.opExtrude","SWEPT_EDGE",EDGE,{"disambiguationData":[OSD([sQuery(id+"F16.wireOp",EDGE,"E26.0"),sQuery(id+"F16.wireOp",EDGE,"E26.1")])]});
            var Q18;
            Q18=makeQuery(id+"F17.opExtrude","SWEPT_EDGE",EDGE,{"disambiguationData":[OSD([sQuery(id+"F16.wireOp",EDGE,"E26.2"),sQuery(id+"F16.wireOp",EDGE,"E26.3")])]});
            var Q19;
            Q19=makeQuery(id+"F17.opExtrude","SWEPT_EDGE",EDGE,{"disambiguationData":[OSD([sQuery(id+"F16.wireOp",EDGE,"E26.1"),sQuery(id+"F16.wireOp",EDGE,"E26.2")])]});
            fillet(context, id + "F20", {"entities" : qUnion([Q0, Q1, Q2, Q3, Q4, Q5, Q6, Q7, Q8, Q9, Q10, Q11, Q12, Q13, Q14, Q15, Q16, Q17, Q18, Q19]), "radius" : 1.14 * mm, "tangentPropagation" : true, "allowEdgeOverflow" : false});
        }
        {
            var Q0;
            Q0=makeQuery(id+"F1.opExtrude","CAP_FACE",FACE,{"disambiguationData":[OSD([sQuery(id+"F0.wireOp",EDGE,"E0.bottom"),sQuery(id+"F0.wireOp",EDGE,"E0.top"),sQuery(id+"F0.wireOp",EDGE,"E0.left"),sQuery(id+"F0.wireOp",EDGE,"E0.right"),sQuery(id+"F0.wireOp",EDGE,"E1.filletArc"),sQuery(id+"F0.wireOp",EDGE,"E2.filletArc"),sQuery(id+"F0.wireOp",EDGE,"E3.bottom"),sQuery(id+"F0.wireOp",EDGE,"E3.top"),sQuery(id+"F0.wireOp",EDGE,"E3.left"),sQuery(id+"F0.wireOp",EDGE,"E3.right"),sQuery(id+"F0.wireOp",EDGE,"E4.filletArc"),sQuery(id+"F0.wireOp",EDGE,"E5.filletArc"),sQuery(id+"F0.wireOp",EDGE,"E6.filletArc"),sQuery(id+"F0.wireOp",EDGE,"E7.filletArc"),sQuery(id+"F0.wireOp",EDGE,"E8.1.0.5"),sQuery(id+"F0.wireOp",EDGE,"E8.1.0.6"),sQuery(id+"F0.wireOp",EDGE,"E8.1.0.7"),sQuery(id+"F0.wireOp",EDGE,"E8.1.0.8"),sQuery(id+"F0.wireOp",EDGE,"E8.1.0.9"),sQuery(id+"F0.wireOp",EDGE,"E8.1.0.10"),sQuery(id+"F0.wireOp",EDGE,"E8.1.0.11"),sQuery(id+"F0.wireOp",EDGE,"E8.1.0.12"),sQuery(id+"F0.wireOp",EDGE,"E8.2.0.5"),sQuery(id+"F0.wireOp",EDGE,"E8.2.0.6"),sQuery(id+"F0.wireOp",EDGE,"E8.2.0.7"),sQuery(id+"F0.wireOp",EDGE,"E8.2.0.8"),sQuery(id+"F0.wireOp",EDGE,"E8.2.0.9"),sQuery(id+"F0.wireOp",EDGE,"E8.2.0.10"),sQuery(id+"F0.wireOp",EDGE,"E8.2.0.11"),sQuery(id+"F0.wireOp",EDGE,"E8.2.0.12"),sQuery(id+"F0.wireOp",EDGE,"E8.3.0.5"),sQuery(id+"F0.wireOp",EDGE,"E8.3.0.6"),sQuery(id+"F0.wireOp",EDGE,"E8.3.0.7"),sQuery(id+"F0.wireOp",EDGE,"E8.3.0.8"),sQuery(id+"F0.wireOp",EDGE,"E8.3.0.9"),sQuery(id+"F0.wireOp",EDGE,"E8.3.0.10"),sQuery(id+"F0.wireOp",EDGE,"E8.3.0.11"),sQuery(id+"F0.wireOp",EDGE,"E8.3.0.12"),sQuery(id+"F0.wireOp",EDGE,"E8.4.0.5"),sQuery(id+"F0.wireOp",EDGE,"E8.4.0.6"),sQuery(id+"F0.wireOp",EDGE,"E8.4.0.7"),sQuery(id+"F0.wireOp",EDGE,"E8.4.0.8"),sQuery(id+"F0.wireOp",EDGE,"E8.4.0.9"),sQuery(id+"F0.wireOp",EDGE,"E8.4.0.10"),sQuery(id+"F0.wireOp",EDGE,"E8.4.0.11"),sQuery(id+"F0.wireOp",EDGE,"E8.4.0.12"),sQuery(id+"F0.wireOp",EDGE,"E8.5.0.5"),sQuery(id+"F0.wireOp",EDGE,"E8.5.0.6"),sQuery(id+"F0.wireOp",EDGE,"E8.5.0.7"),sQuery(id+"F0.wireOp",EDGE,"E8.5.0.8"),sQuery(id+"F0.wireOp",EDGE,"E8.5.0.9"),sQuery(id+"F0.wireOp",EDGE,"E8.5.0.10"),sQuery(id+"F0.wireOp",EDGE,"E8.5.0.11"),sQuery(id+"F0.wireOp",EDGE,"E8.5.0.12"),sQuery(id+"F0.wireOp",EDGE,"E8.6.0.5"),sQuery(id+"F0.wireOp",EDGE,"E8.6.0.6"),sQuery(id+"F0.wireOp",EDGE,"E8.6.0.7"),sQuery(id+"F0.wireOp",EDGE,"E8.6.0.8"),sQuery(id+"F0.wireOp",EDGE,"E8.6.0.9"),sQuery(id+"F0.wireOp",EDGE,"E8.6.0.10"),sQuery(id+"F0.wireOp",EDGE,"E8.6.0.11"),sQuery(id+"F0.wireOp",EDGE,"E8.6.0.12"),sQuery(id+"F0.wireOp",EDGE,"E8.7.0.5"),sQuery(id+"F0.wireOp",EDGE,"E8.7.0.6"),sQuery(id+"F0.wireOp",EDGE,"E8.7.0.7"),sQuery(id+"F0.wireOp",EDGE,"E8.7.0.8"),sQuery(id+"F0.wireOp",EDGE,"E8.7.0.9"),sQuery(id+"F0.wireOp",EDGE,"E8.7.0.10"),sQuery(id+"F0.wireOp",EDGE,"E8.7.0.11"),sQuery(id+"F0.wireOp",EDGE,"E8.7.0.12"),sQuery(id+"F0.wireOp",EDGE,"E8.8.0.5"),sQuery(id+"F0.wireOp",EDGE,"E8.8.0.6"),sQuery(id+"F0.wireOp",EDGE,"E8.8.0.7"),sQuery(id+"F0.wireOp",EDGE,"E8.8.0.8"),sQuery(id+"F0.wireOp",EDGE,"E8.8.0.9"),sQuery(id+"F0.wireOp",EDGE,"E8.8.0.10"),sQuery(id+"F0.wireOp",EDGE,"E8.8.0.11"),sQuery(id+"F0.wireOp",EDGE,"E8.8.0.12"),sQuery(id+"F0.wireOp",EDGE,"E8.9.0.5"),sQuery(id+"F0.wireOp",EDGE,"E8.9.0.6"),sQuery(id+"F0.wireOp",EDGE,"E8.9.0.7"),sQuery(id+"F0.wireOp",EDGE,"E8.9.0.8"),sQuery(id+"F0.wireOp",EDGE,"E8.9.0.9"),sQuery(id+"F0.wireOp",EDGE,"E8.9.0.10"),sQuery(id+"F0.wireOp",EDGE,"E8.9.0.11"),sQuery(id+"F0.wireOp",EDGE,"E8.9.0.12"),sQuery(id+"F0.wireOp",EDGE,"E8.10.0.5"),sQuery(id+"F0.wireOp",EDGE,"E8.10.0.6"),sQuery(id+"F0.wireOp",EDGE,"E8.10.0.7"),sQuery(id+"F0.wireOp",EDGE,"E8.10.0.8"),sQuery(id+"F0.wireOp",EDGE,"E8.10.0.9"),sQuery(id+"F0.wireOp",EDGE,"E8.10.0.10"),sQuery(id+"F0.wireOp",EDGE,"E8.10.0.11"),sQuery(id+"F0.wireOp",EDGE,"E8.10.0.12"),sQuery(id+"F0.wireOp",EDGE,"E8.11.0.5"),sQuery(id+"F0.wireOp",EDGE,"E8.11.0.6"),sQuery(id+"F0.wireOp",EDGE,"E8.11.0.7"),sQuery(id+"F0.wireOp",EDGE,"E8.11.0.8"),sQuery(id+"F0.wireOp",EDGE,"E8.11.0.9"),sQuery(id+"F0.wireOp",EDGE,"E8.11.0.10"),sQuery(id+"F0.wireOp",EDGE,"E8.11.0.11"),sQuery(id+"F0.wireOp",EDGE,"E8.11.0.12"),sQuery(id+"F0.wireOp",EDGE,"E8.12.0.5"),sQuery(id+"F0.wireOp",EDGE,"E8.12.0.6"),sQuery(id+"F0.wireOp",EDGE,"E8.12.0.7"),sQuery(id+"F0.wireOp",EDGE,"E8.12.0.8"),sQuery(id+"F0.wireOp",EDGE,"E8.12.0.9"),sQuery(id+"F0.wireOp",EDGE,"E8.12.0.10"),sQuery(id+"F0.wireOp",EDGE,"E8.12.0.11"),sQuery(id+"F0.wireOp",EDGE,"E8.12.0.12")])],"isStart":false});
            var sketch = newSketch(context, id + "F21", { "sketchPlane" : qUnion([Q0])});
            skText(sketch, "E29", { "text": "AS", "fontName": "OpenSans-Regular.ttf"});
            const initialGuessF21  = {"E29": [0.01472, 0.00238, 0, 1, 0.00889]};
            skSetInitialGuess(sketch, initialGuessF21);
            skSolve(sketch);
        }
        {
            var Q0;
            Q0 = qSketchRegion(id + "F21", true);
            extrude(context, id + "F22", {"entities" : qUnion([Q0]), "operationType" : NewBodyOperationType.ADD, "depth" : 1.27 * mm, "offsetDistance" : 25.4 * mm});
        }
        {
            var Q0;
            Q0=makeQuery(id+"F15.boolean.opBoolean","MERGE",FACE,{"derivedFrom":[makeQuery(id+"F13.boolean.opBoolean","MERGE",FACE,{"derivedFrom":[makeQuery(id+"F8.opExtrude","CAP_FACE",FACE,{"disambiguationData":[OSD([sQuery(id+"F7.wireOp",EDGE,"E12.bottom"),sQuery(id+"F7.wireOp",EDGE,"E12.top"),sQuery(id+"F7.wireOp",EDGE,"E12.left"),sQuery(id+"F7.wireOp",EDGE,"E12.right")])],"isStart":false}),makeQuery(id+"F13.opExtrude","SWEPT_FACE",FACE,{"disambiguationData":[OSD([sQuery(id+"F12.wireOp",EDGE,"E18")])]})]}),makeQuery(id+"F15.opExtrude","SWEPT_FACE",FACE,{"disambiguationData":[OSD([sQuery(id+"F14.wireOp",EDGE,"E22")])]})]});
            var sketch = newSketch(context, id + "F23", { "sketchPlane" : qUnion([Q0])});
            skText(sketch, "E30", { "text": "AS", "fontName": "OpenSans-Regular.ttf"});
            const initialGuessF23  = {"E30": [0.01472, 0.02829, 0, 1, 0.0089]};
            skSetInitialGuess(sketch, initialGuessF23);
            skSolve(sketch);
        }
        {
            var Q0;
            Q0 = qSketchRegion(id + "F23", true);
            extrude(context, id + "F24", {"entities" : qUnion([Q0]), "operationType" : NewBodyOperationType.ADD, "depth" : 1.27 * mm, "offsetDistance" : 25.4 * mm});
        }
    });
